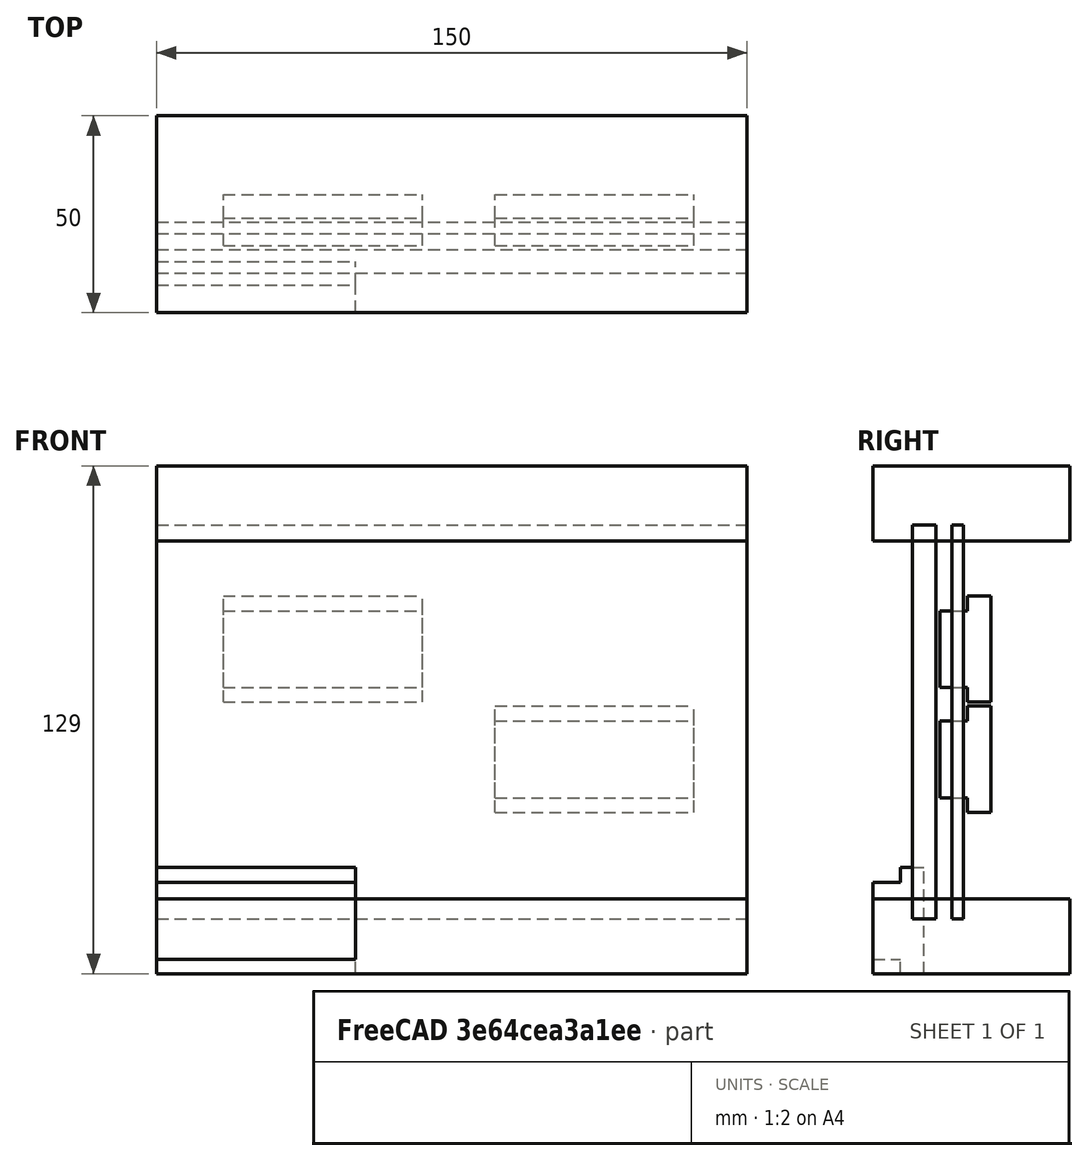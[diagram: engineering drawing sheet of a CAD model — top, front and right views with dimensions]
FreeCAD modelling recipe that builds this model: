
FCSTD DOCUMENT  (FreeCAD 0.14R3702 (Git))
Label: stand
License: CC-BY 3.0
LicenseURL: http://creativecommons.org/licenses/by/3.0/
objects: Part::Box×5, Part::Feature×3, App::DocumentObjectGroup×2, Part::MultiFuse×1
note: 9 computed .brp shape members not serialized (recipe doc carries the construction recipe); baked Part::Feature solids carry a one-line shape summary decoded from their .brp

FEATURE [Part::Box] Box  label="Frontpanel"
  Height = 100
  Length = 150
  Placement = pos=(0,10,14) rot=(0,0,1;0rad)
  Width = 6
FEATURE [Part::Box] Box001  label="Displayframe"
  Height = 100
  Length = 150
  Placement = pos=(0,20,14) rot=(0,0,1;0rad)
  Width = 3
FEATURE [Part::Box] Box002  label="Bottom"
  Height = 19
  Length = 150
  Width = 50
FEATURE [Part::Feature] Box002001  label="Top"
  Placement = pos=(0,0,110) rot=(0,0,1;0rad)
  shape: bbox 150 x 50 x 19 mm, 6 faces (baked)
FEATURE [Part::Box] Box002002  label="7Segment"
  Height = 19.5
  Length = 50.5
  Placement = pos=(0,0,3.7) rot=(0,0,1;0rad)
  Width = 7
FEATURE [Part::Box] Box002003  label="PCB"
  Height = 27
  Length = 50.5
  Placement = pos=(0,7,0) rot=(0,0,1;0rad)
  Width = 6
FEATURE [Part::MultiFuse] Fusion  label="7SegmentBackpack"
  Shapes = -> [Box002003,Box002002]
FEATURE [App::DocumentObjectGroup] Gruppe  label="Displays"
  Group = -> [Box002002,Box002003,Fusion]
FEATURE [App::DocumentObjectGroup] Gruppe001  label="raw-models"
  Group = -> [Box002001,Box002,Box001,Box,Gruppe]
FEATURE [Part::Feature] Fusion_solid  label="Time-Display"
  Placement = pos=(86,17,41) rot=(0,0,1;0rad)
  shape: bbox 50.5 x 13 x 27 mm, 12 faces (baked)
FEATURE [Part::Feature] Fusion_solid001  label="Temerature-Display"
  Placement = pos=(17,17,69) rot=(0,0,1;0rad)
  shape: bbox 50.5 x 13 x 27 mm, 12 faces (baked)
